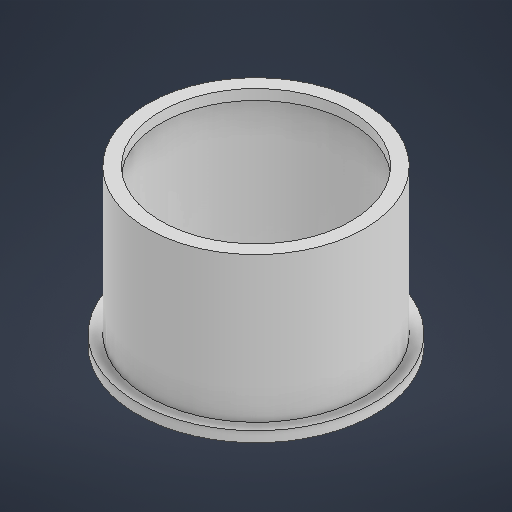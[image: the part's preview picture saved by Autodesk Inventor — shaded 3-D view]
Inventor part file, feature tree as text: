
AUTODESK INVENTOR PART (.ipt)
format: ipt  version: 2025 (Build 290162000, 162)  size: 320,000 bytes
history: native  units: in
note: dims shown in document units (in); Inventor stores cm internally (conversion verified against a paired STEP export)
features: other x12, extrude x8, sketch x6, fillet x5, plane x1
ambient origin geometry x8: Origin, YZ Plane, XZ Plane, XY Plane, X Axis, Y Axis, Z Axis, Center Point
bodies: Solid1 (feature_tree)
feature tree (32):
  other  "Table"
  other  "Cylinder Segment - 01"
  other  "Cylinder Segment - 02"
  other  "Cylinder Segment - 03"
  other  "Cylinder Segment - 04"
  other  "Cylinder Segment - 05"
  other  "Cylinder Segment - 06"
  other  "Cylinder Segment - 07"
  other  "Cylinder Segment - 08"
  other  "Cylinder Segment - 09"
  other  "Cylinder Segment - 10"
  other  "Cylinder Segment - Face"
  sketch  "Sketch1"  dims[d5=0.0in d7=0.0in]
  extrude  "Extrusion1"  TaperAngle=0.0deg  [1 undecoded]
  extrude  "Extrusion2"  Depth=10.0394in
  extrude  "Extrusion7"  Depth=0.3937in
  plane  "Work Plane2"
  extrude  "Extrusion8"  Depth=3.937in TaperAngle=360.0deg
  sketch  "Sketch24"  dims[d234=0.0787in d235=2.5591in]
  extrude  "Extrusion30"  Depth=2.5591in
  extrude  "Extrusion31"  Depth=0.3937in
  extrude  "Extrusion32"  Depth=0.3937in
  fillet  "Fillet14"  Radius=10.6299in
  fillet  "Fillet15"  Radius=3.5433in
  fillet  "Fillet16"  Radius=6.033in
  fillet  "Fillet17"  Radius=8.9897in
  fillet  "Fillet18"  Radius=0.0787in
  extrude  "Extrusion33"  Depth=0.3937in
  sketch  "Sketch2"  dims[d18=0.0in d27=10.0394in]
  sketch  "Sketch3"  dims[d33=0.3937in d34=0.0in d52=4.5276in]
  sketch  "Sketch Circular Pattern4"  dims[d229=0.2165in d230=3.937in d232=360.0deg]
  sketch  "Sketch25"  dims[d237=0.0591in d238=0.4375in d240=0.8253in d241=10.6299in d242=3.5433in d243=6.033in d244=8.9897in d247=0.0787in d248=5.1083in d249=3.6614in d250=0.0in d251=3.6614in d252=0.0in d253=9.4488in d254=0.3937in d255=0.0in d256=0.3937in d257=0.3937in d258=0.0787in d259=0.1969in d260=0.1969in d261=0.3937in d262=0.0in d113=0.0197in d114=0.0344in d115=0.0197in d116=0.0344in d167=0.0197in d168=0.0344in d169=0.0197in d170=0.0344in d215=0.0197in d216=0.0344in d217=0.0197in d218=0.0344in d219=0.0in d220=0.0in]
note: 1 required parameter value undecoded (feature->parameter linkage not recoverable at this tier; creation-order binding heuristic only, values carry confidence <= 0.55)
